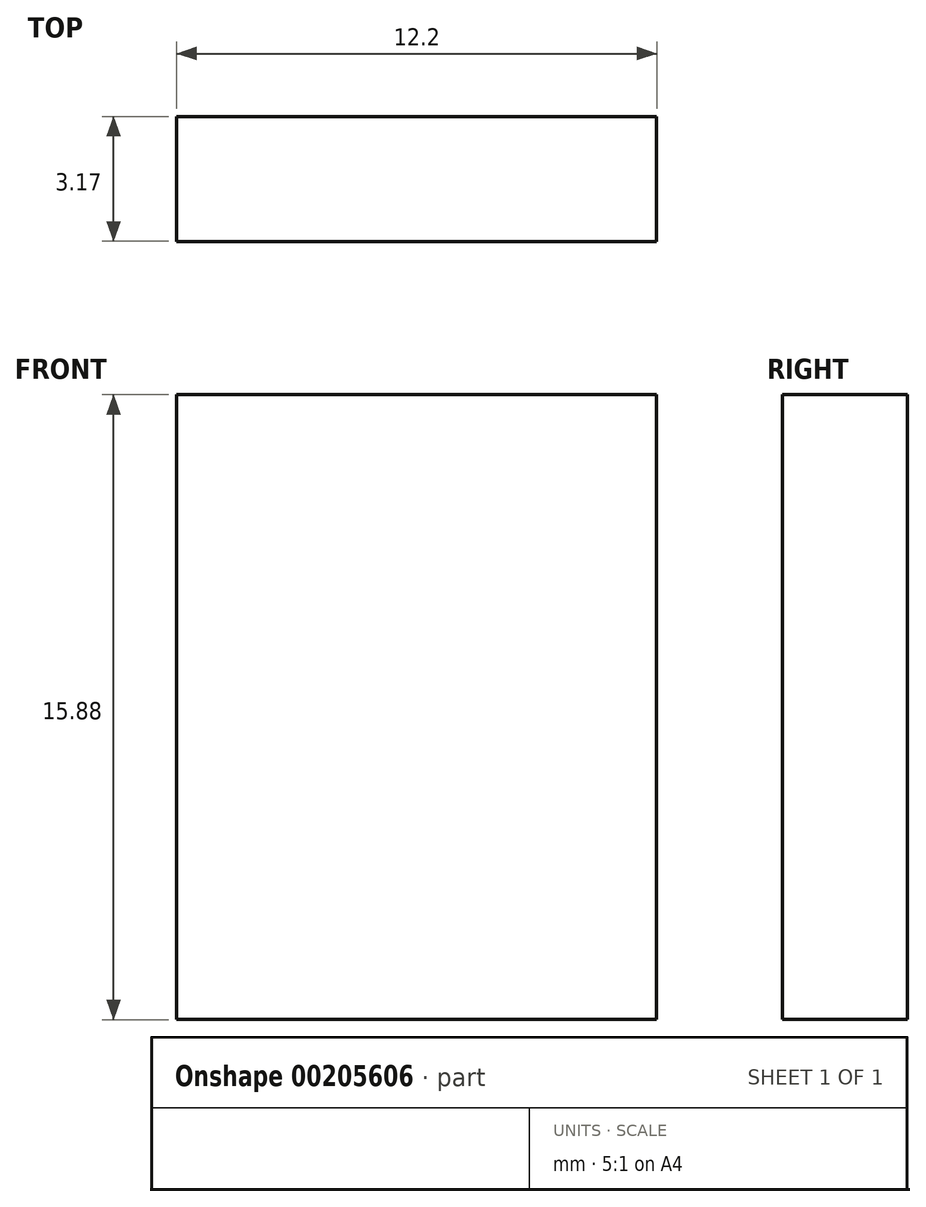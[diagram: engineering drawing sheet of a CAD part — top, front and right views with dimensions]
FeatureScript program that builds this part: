
annotation { "Feature Type Name" : "Feature", "Feature Type Description" : "" }
export const myFeature = defineFeature(function(context is Context, id is Id, definition is map)
    precondition{}
    {
        {
            var Q0;
            Q0=qCreatedBy(makeId("Front.planeOp"),FACE);
            var sketch = newSketch(context, id + "F0", { "sketchPlane" : qUnion([Q0])});
            skLineSegment(sketch, "E0.bottom", {"start": v(-6.1, 7.94) * mm, "end": v(6.1, 7.94) * mm});
            skLineSegment(sketch, "E0.top", {"start": v(-6.1, -7.94) * mm, "end": v(6.1, -7.94) * mm});
            skLineSegment(sketch, "E0.left", {"start": v(-6.1, 7.94) * mm, "end": v(-6.1, -7.94) * mm});
            skLineSegment(sketch, "E0.right", {"start": v(6.1, 7.94) * mm, "end": v(6.1, -7.94) * mm});
            skPoint(sketch, "E0.middle", {"position": v(0, 0) * mm});
            skSolve(sketch);
        }
        {
            var Q0;
            Q0=qSketchRegion(id+"F0",true);
            extrude(context, id + "F1", {"entities" : qUnion([Q0]), "flatOperationType" : FlatOperationType.REMOVE, "offsetDistance" : 25.4 * mm, "depth" : 3.17 * mm, "domain" : OperationDomain.MODEL});
        }
    });
